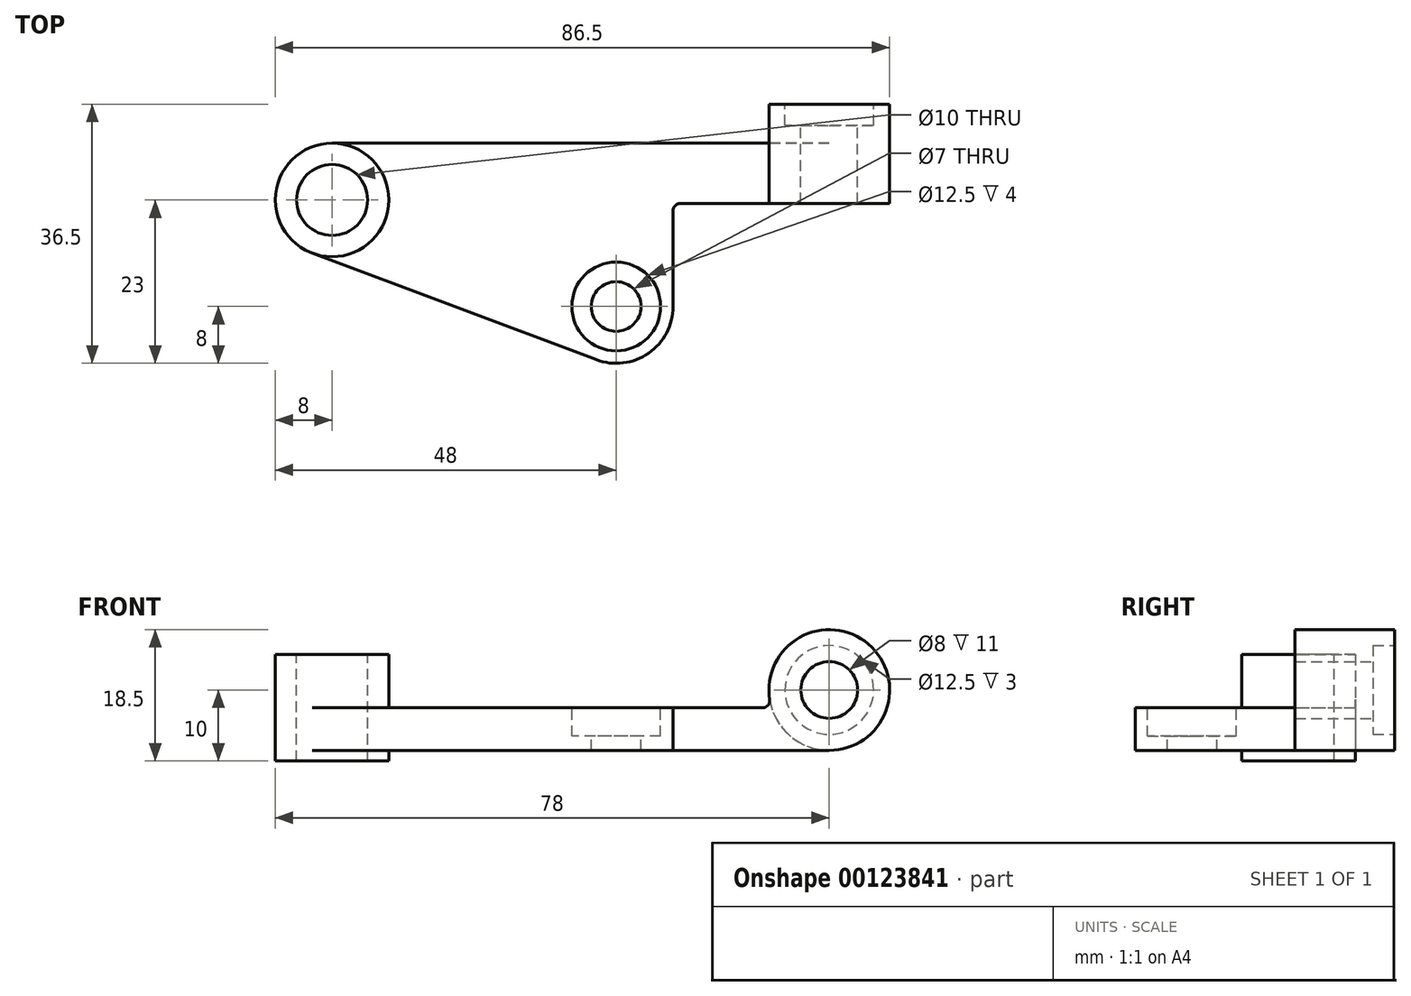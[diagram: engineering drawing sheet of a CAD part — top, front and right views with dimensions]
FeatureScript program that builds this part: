
annotation { "Feature Type Name" : "Feature", "Feature Type Description" : "" }
export const myFeature = defineFeature(function(context is Context, id is Id, definition is map)
    precondition{}
    {
        {
            var Q0;
            Q0=qCreatedBy(makeId("Top.planeOp"),FACE);
            var sketch = newSketch(context, id + "F0", { "sketchPlane" : qUnion([Q0])});
            skLineSegment(sketch, "E0", {"start": v(0, 0) * mm, "end": v(-70, 0) * mm});
            skArc(sketch, "E1", {"start": v(-70, 0) * mm, "mid": v(-77.87, -6.57) * mm, "end": v(-72.8, -15.5) * mm});
            skLineSegment(sketch, "E2", {"start": v(-72.8, -15.5) * mm, "end": v(-32.8, -30.5) * mm});
            skArc(sketch, "E3", {"start": v(-32.8, -30.5) * mm, "mid": v(-25.44, -29.58) * mm, "end": v(-22, -23) * mm});
            skLineSegment(sketch, "E4", {"start": v(-22, -23) * mm, "end": v(-22, -8.5) * mm});
            skLineSegment(sketch, "E5", {"start": v(-22, -8.5) * mm, "end": v(0, -8.5) * mm});
            skLineSegment(sketch, "E6", {"start": v(0, -8.5) * mm, "end": v(0, 0) * mm});
            skSolve(sketch);
        }
        {
            var Q0;
            Q0=makeQuery(id+"F0.imprint","IMPRINT",FACE,{"disambiguationData":[TD([[makeQuery(id+"F0.imprint","IMPRINT",EDGE,{"derivedFrom":sQuery(id+"F0.wireOp",EDGE,"E0")}),1.0]])]});
            extrude(context, id + "F1", {"entities" : qUnion([Q0]), "depth" : 6 * mm});
        }
        {
            var Q0;
            Q0=makeQuery(id+"F1.opExtrude","SWEPT_FACE",FACE,{"disambiguationData":[OSD([sQuery(id+"F0.wireOp",EDGE,"E5")])]});
            var sketch = newSketch(context, id + "F2", { "sketchPlane" : qUnion([Q0])});
            skCircle(sketch, "E7", {"center": v(0, 8.5) * mm, "radius": 8.5 * mm});
            skPoint(sketch, "E7.centerSnap0", {"position": v(0, 3) * mm});
            skSolve(sketch);
        }
        {
            var Q0;
            {var subQ1=sQuery(id+"F0.wireOp",EDGE,"E5");var subQ2=makeQuery(id+"F1.opExtrude","SWEPT_EDGE",EDGE,{"disambiguationData":[OSD([subQ1,sQuery(id+"F0.wireOp",EDGE,"E6")])]});Q0=makeQuery(id+"F2.imprint","IMPRINT",FACE,{"disambiguationData":[TD([[makeQuery(id+"F2.imprint","IMPRINT",EDGE,{"derivedFrom":subQ2}),1.0]])]});}
            var Q1;
            {var subQ1=sQuery(id+"F0.wireOp",EDGE,"E5");var subQ2=makeQuery(id+"F1.opExtrude","SWEPT_EDGE",EDGE,{"disambiguationData":[OSD([subQ1,sQuery(id+"F0.wireOp",EDGE,"E6")])]});Q1=makeQuery(id+"F2.imprint","IMPRINT",FACE,{"disambiguationData":[TD([[makeQuery(id+"F2.imprint","IMPRINT",EDGE,{"derivedFrom":subQ2}),-1.0]])]});}
            extrude(context, id + "F3", {"entities" : qUnion([Q0, Q1]), "operationType" : NewBodyOperationType.ADD, "oppositeDirection" : true, "depth" : 14 * mm});
        }
        {
            var Q0;
            Q0=sQuery(id+"F2.wireOp",VERTEX,"E7.center");
            var Q1;
            Q1=makeQuery(id+"F1.opExtrude","CAP_FACE",FACE,{"disambiguationData":[OSD([sQuery(id+"F0.wireOp",EDGE,"E0"),sQuery(id+"F0.wireOp",EDGE,"E1"),sQuery(id+"F0.wireOp",EDGE,"E2"),sQuery(id+"F0.wireOp",EDGE,"E3"),sQuery(id+"F0.wireOp",EDGE,"E4"),sQuery(id+"F0.wireOp",EDGE,"E5"),sQuery(id+"F0.wireOp",EDGE,"E6")])],"isStart":false});
            cPlane(context, id + "F4", {"entities" : qUnion([Q0, Q1]), "cplaneType" : CPlaneType.PLANE_POINT, "offset" : 25 * mm, "width" : 150 * mm, "height" : 150 * mm});
        }
        {
            var Q0;
            Q0=qCreatedBy(id+"F4.planeOp",FACE);
            cPlane(context, id + "F5", {"entities" : qUnion([Q0]), "cplaneType" : CPlaneType.OFFSET, "offset" : 5 * mm, "width" : 150 * mm, "height" : 150 * mm});
        }
        {
            var Q0;
            Q0=qCreatedBy(id+"F5.planeOp",FACE);
            cPlane(context, id + "F6", {"entities" : qUnion([Q0]), "cplaneType" : CPlaneType.OFFSET, "offset" : 15 * mm, "oppositeDirection" : true, "width" : 150 * mm, "height" : 150 * mm});
        }
        {
            var Q0;
            Q0=makeQuery(id+"F1.opExtrude","CAP_FACE",FACE,{"disambiguationData":[OSD([sQuery(id+"F0.wireOp",EDGE,"E0"),sQuery(id+"F0.wireOp",EDGE,"E1"),sQuery(id+"F0.wireOp",EDGE,"E2"),sQuery(id+"F0.wireOp",EDGE,"E3"),sQuery(id+"F0.wireOp",EDGE,"E4"),sQuery(id+"F0.wireOp",EDGE,"E5"),sQuery(id+"F0.wireOp",EDGE,"E6")])],"isStart":false});
            var sketch = newSketch(context, id + "F7", { "sketchPlane" : qUnion([Q0])});
            skCircle(sketch, "E8", {"center": v(-70, -8) * mm, "radius": 8 * mm});
            skSolve(sketch);
        }
        {
            var Q0;
            {var subQ0=sQuery(id+"F7.wireOp",EDGE,"E8");var subQ3=sQuery(id+"F0.wireOp",EDGE,"E2");var subQ6=makeQuery(id+"F7.imprint","INTERSECT",VERTEX,{"derivedFrom":[makeQuery(id+"F1.opExtrude","CAP_EDGE",EDGE,{"disambiguationData":[OSD([subQ3])],"isStart":false}),subQ0]});Q0=makeQuery(id+"F7.imprint","IMPRINT",FACE,{"disambiguationData":[TD([[makeQuery(id+"F7.imprint","IMPRINT",EDGE,{"disambiguationData":[TD([[subQ6,1.0]])],"derivedFrom":subQ0}),1.0]])]});}
            var Q1;
            Q1=qCreatedBy(id+"F5.planeOp",FACE);
            var Q2;
            Q2=qCreatedBy(id+"F6.planeOp",FACE);
            extrude(context, id + "F8", {"entities" : qUnion([Q0]), "operationType" : NewBodyOperationType.ADD, "endBound" : BoundingType.UP_TO_SURFACE, "endBoundEntityFace" : qUnion([Q1]), "depth" : 25 * mm, "hasSecondDirection" : true, "secondDirectionBound" : SecondDirectionBoundingType.UP_TO_SURFACE, "secondDirectionOppositeDirection" : true, "secondDirectionBoundEntityFace" : qUnion([Q2]), "secondDirectionDepth" : 25 * mm});
        }
        {
            var Q0;
            Q0=makeQuery(id+"F3.opExtrude","CAP_FACE",FACE,{"disambiguationData":[OSD([sQuery(id+"F2.wireOp",EDGE,"E7")])],"isStart":false});
            var sketch = newSketch(context, id + "F9", { "sketchPlane" : qUnion([Q0])});
            skPoint(sketch, "E9", {"position": v(0, 8.5) * mm});
            skSolve(sketch);
        }
        {
            var Q0;
            Q0=sQuery(id+"F9.wireOp",VERTEX,"E9");
            var Q1;
            Q1=makeQuery(id+"F1.opExtrude","SWEPT_BODY",BODY,{"disambiguationData":[OSD([sQuery(id+"F0.wireOp",EDGE,"E0"),sQuery(id+"F0.wireOp",EDGE,"E1"),sQuery(id+"F0.wireOp",EDGE,"E2"),sQuery(id+"F0.wireOp",EDGE,"E3"),sQuery(id+"F0.wireOp",EDGE,"E4"),sQuery(id+"F0.wireOp",EDGE,"E5"),sQuery(id+"F0.wireOp",EDGE,"E6")])]});
            hole(context, id + "F10", {"style" : HoleStyle.C_BORE, "endStyle" : HoleEndStyle.THROUGH, "standardTappedOrClearance" : lookupTablePath({ "standard" : "ISO", "size" : "8", "type" : "Drilled" }), "standardBlindInLast" : lookupTablePath({ "standard" : "ISO", "size" : "8", "type" : "Drilled" }), "holeDiameter" : 8 * mm, "cBoreDiameter" : 12.5 * mm, "cBoreDepth" : 3 * mm, "locations" : qUnion([Q0]), "scope" : qUnion([Q1]), "isTappedThrough" : true});
        }
        {
            var Q0;
            Q0=makeQuery(id+"F8.opExtrude","CAP_FACE",FACE,{"disambiguationData":[OSD([sQuery(id+"F7.wireOp",EDGE,"E8")])],"isStart":false});
            var sketch = newSketch(context, id + "F11", { "sketchPlane" : qUnion([Q0])});
            skPoint(sketch, "E10", {"position": v(-70, -8) * mm});
            skSolve(sketch);
        }
        {
            var Q0;
            Q0=sQuery(id+"F11.wireOp",VERTEX,"E10");
            var Q1;
            Q1=makeQuery(id+"F1.opExtrude","SWEPT_BODY",BODY,{"disambiguationData":[OSD([sQuery(id+"F0.wireOp",EDGE,"E0"),sQuery(id+"F0.wireOp",EDGE,"E1"),sQuery(id+"F0.wireOp",EDGE,"E2"),sQuery(id+"F0.wireOp",EDGE,"E3"),sQuery(id+"F0.wireOp",EDGE,"E4"),sQuery(id+"F0.wireOp",EDGE,"E5"),sQuery(id+"F0.wireOp",EDGE,"E6")])]});
            hole(context, id + "F12", {"style" : HoleStyle.SIMPLE, "endStyle" : HoleEndStyle.THROUGH, "standardTappedOrClearance" : lookupTablePath({ "standard" : "ISO", "size" : "10", "type" : "Drilled" }), "standardBlindInLast" : lookupTablePath({ "standard" : "ISO", "size" : "10", "type" : "Drilled" }), "holeDiameter" : 10 * mm, "locations" : qUnion([Q0]), "scope" : qUnion([Q1]), "isTappedThrough" : true});
        }
        {
            var Q0;
            Q0=makeQuery(id+"F1.opExtrude","CAP_FACE",FACE,{"disambiguationData":[OSD([sQuery(id+"F0.wireOp",EDGE,"E0"),sQuery(id+"F0.wireOp",EDGE,"E1"),sQuery(id+"F0.wireOp",EDGE,"E2"),sQuery(id+"F0.wireOp",EDGE,"E3"),sQuery(id+"F0.wireOp",EDGE,"E4"),sQuery(id+"F0.wireOp",EDGE,"E5"),sQuery(id+"F0.wireOp",EDGE,"E6")])],"isStart":false});
            var sketch = newSketch(context, id + "F13", { "sketchPlane" : qUnion([Q0])});
            skPoint(sketch, "E11", {"position": v(-30, -23) * mm});
            skSolve(sketch);
        }
        {
            var Q0;
            Q0=sQuery(id+"F13.wireOp",VERTEX,"E11");
            var Q1;
            Q1=makeQuery(id+"F1.opExtrude","SWEPT_BODY",BODY,{"disambiguationData":[OSD([sQuery(id+"F0.wireOp",EDGE,"E0"),sQuery(id+"F0.wireOp",EDGE,"E1"),sQuery(id+"F0.wireOp",EDGE,"E2"),sQuery(id+"F0.wireOp",EDGE,"E3"),sQuery(id+"F0.wireOp",EDGE,"E4"),sQuery(id+"F0.wireOp",EDGE,"E5"),sQuery(id+"F0.wireOp",EDGE,"E6")])]});
            hole(context, id + "F14", {"style" : HoleStyle.C_BORE, "endStyle" : HoleEndStyle.THROUGH, "holeDiameter" : 7 * mm, "cBoreDiameter" : 12.5 * mm, "cBoreDepth" : 4 * mm, "locations" : qUnion([Q0]), "scope" : qUnion([Q1]), "isTappedThrough" : true});
        }
        {
            var Q0;
            Q0=makeQuery(id+"F1.opExtrude","SWEPT_EDGE",EDGE,{"disambiguationData":[OSD([sQuery(id+"F0.wireOp",EDGE,"E4"),sQuery(id+"F0.wireOp",EDGE,"E5")])]});
            var Q1;
            Q1=makeQuery(id+"F3.boolean.opBoolean","INTERSECT",EDGE,{"derivedFrom":[makeQuery(id+"F1.opExtrude","CAP_FACE",FACE,{"disambiguationData":[OSD([sQuery(id+"F0.wireOp",EDGE,"E0"),sQuery(id+"F0.wireOp",EDGE,"E1"),sQuery(id+"F0.wireOp",EDGE,"E2"),sQuery(id+"F0.wireOp",EDGE,"E3"),sQuery(id+"F0.wireOp",EDGE,"E4"),sQuery(id+"F0.wireOp",EDGE,"E5"),sQuery(id+"F0.wireOp",EDGE,"E6")])],"isStart":false}),makeQuery(id+"F3.opExtrude","SWEPT_FACE",FACE,{"disambiguationData":[OSD([sQuery(id+"F2.wireOp",EDGE,"E7")])]})]});
            fillet(context, id + "F15", {"entities" : qUnion([Q0, Q1]), "radius" : 1 * mm, "tangentPropagation" : true, "allowEdgeOverflow" : false});
        }
    });
